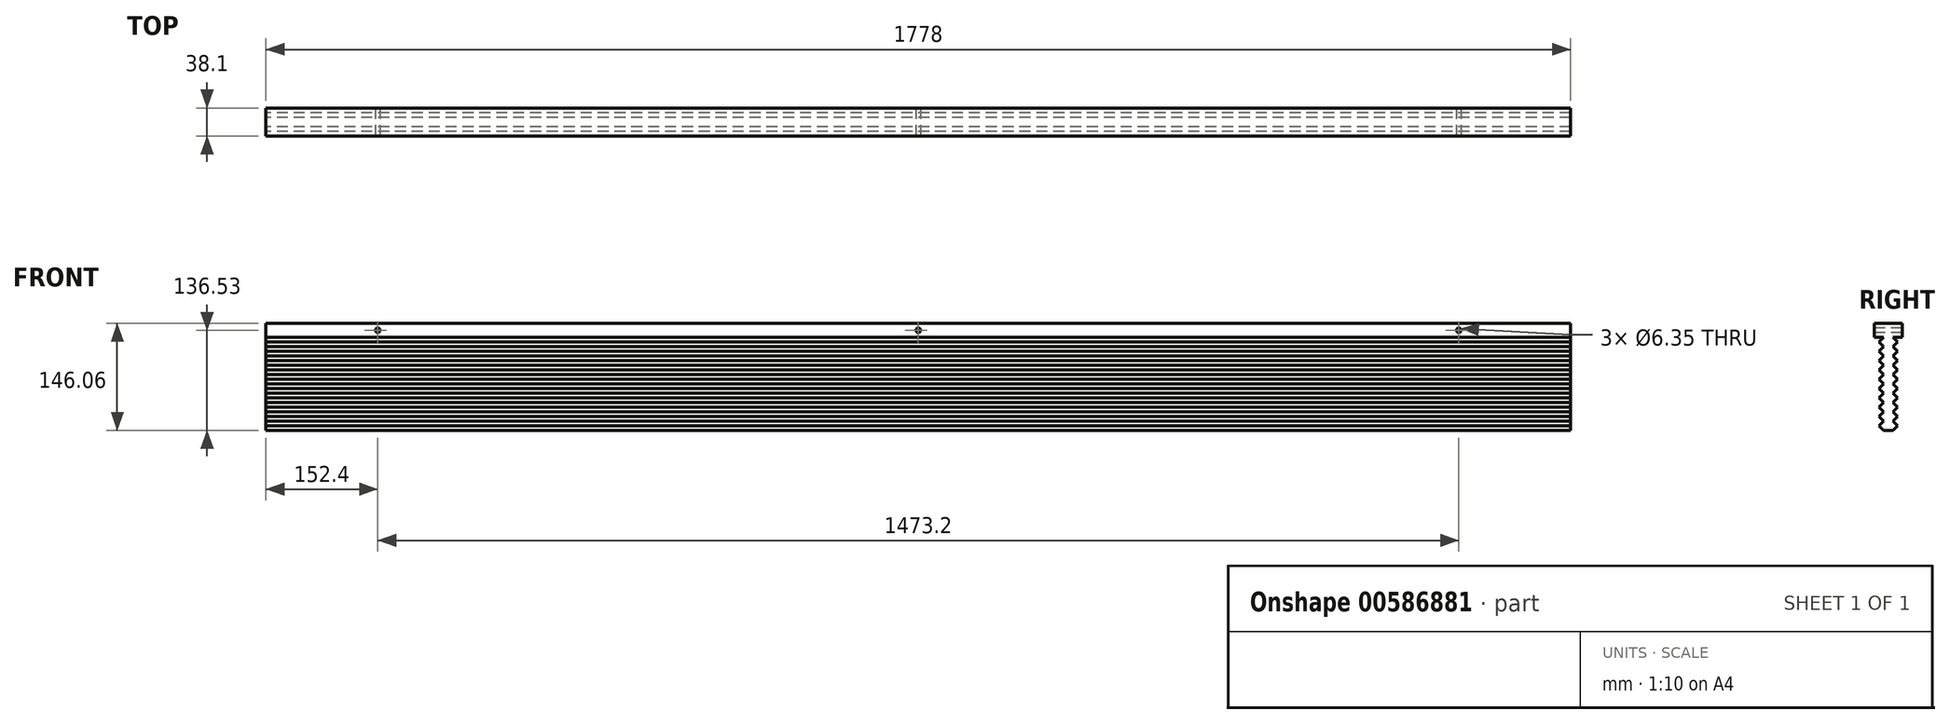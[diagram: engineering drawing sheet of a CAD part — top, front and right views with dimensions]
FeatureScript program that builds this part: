
annotation { "Feature Type Name" : "Feature", "Feature Type Description" : "" }
export const myFeature = defineFeature(function(context is Context, id is Id, definition is map)
    precondition{}
    {
        {
            var Q0;
            Q0=qCreatedBy(makeId("Right.planeOp"),FACE);
            var sketch = newSketch(context, id + "F0", { "sketchPlane" : qUnion([Q0])});
            skLineSegment(sketch, "E0.bottom", {"start": v(-19.05, 9.52) * mm, "end": v(19.05, 9.52) * mm});
            skLineSegment(sketch, "E0.top", {"start": v(-19.05, -9.52) * mm, "end": v(19.05, -9.52) * mm});
            skLineSegment(sketch, "E0.left", {"start": v(-19.05, 9.52) * mm, "end": v(-19.05, -9.52) * mm});
            skLineSegment(sketch, "E0.right", {"start": v(19.05, 9.52) * mm, "end": v(19.05, -9.52) * mm});
            skPoint(sketch, "E0.middle", {"position": v(0, 0) * mm});
            skSolve(sketch);
        }
        {
            var Q0;
            Q0 = qSketchRegion(id + "F0", true);
            extrude(context, id + "F1", {"entities" : qUnion([Q0]), "endBound" : BoundingType.SYMMETRIC, "depth" : 1778 * mm, "offsetDistance" : 25.4 * mm});
        }
        {
            var Q0;
            Q0=qCreatedBy(makeId("Right.planeOp"),FACE);
            var sketch = newSketch(context, id + "F2", { "sketchPlane" : qUnion([Q0])});
            skLineSegment(sketch, "E1", {"start": v(-6.35, -9.52) * mm, "end": v(-12.7, -15.88) * mm});
            skLineSegment(sketch, "E2", {"start": v(-12.7, -15.87) * mm, "end": v(-6.35, -22.22) * mm});
            skLineSegment(sketch, "E3", {"start": v(-6.35, -22.23) * mm, "end": v(0, -22.23) * mm});
            skLineSegment(sketch, "E4", {"start": v(-6.35, -9.52) * mm, "end": v(0, -9.52) * mm});
            skLineSegment(sketch, "E5.MirrorCS", {"start": v(6.35, -9.52) * mm, "end": v(0, -9.52) * mm});
            skLineSegment(sketch, "E6.MirrorCS", {"start": v(6.35, -9.52) * mm, "end": v(12.7, -15.88) * mm});
            skLineSegment(sketch, "E7.MirrorCS", {"start": v(12.7, -15.87) * mm, "end": v(6.35, -22.23) * mm});
            skLineSegment(sketch, "E8.MirrorCS", {"start": v(6.35, -22.23) * mm, "end": v(0, -22.23) * mm});
            skLineSegment(sketch, "E9.1.0.0", {"start": v(-6.35, -34.93) * mm, "end": v(0, -34.93) * mm});
            skLineSegment(sketch, "E9.1.0.1", {"start": v(-12.7, -28.57) * mm, "end": v(-6.35, -34.92) * mm});
            skLineSegment(sketch, "E9.1.0.2", {"start": v(-6.35, -22.22) * mm, "end": v(-12.7, -28.57) * mm});
            skLineSegment(sketch, "E9.1.0.5", {"start": v(6.35, -22.22) * mm, "end": v(12.7, -28.57) * mm});
            skLineSegment(sketch, "E9.1.0.6", {"start": v(12.7, -28.57) * mm, "end": v(6.35, -34.93) * mm});
            skLineSegment(sketch, "E9.1.0.7", {"start": v(6.35, -34.93) * mm, "end": v(0, -34.93) * mm});
            skLineSegment(sketch, "E9.2.0.0", {"start": v(-6.35, -47.63) * mm, "end": v(0, -47.63) * mm});
            skLineSegment(sketch, "E9.2.0.1", {"start": v(-12.7, -41.27) * mm, "end": v(-6.35, -47.62) * mm});
            skLineSegment(sketch, "E9.2.0.2", {"start": v(-6.35, -34.92) * mm, "end": v(-12.7, -41.28) * mm});
            skLineSegment(sketch, "E9.2.0.3", {"start": v(-6.35, -34.93) * mm, "end": v(0, -34.93) * mm});
            skLineSegment(sketch, "E9.2.0.4", {"start": v(6.35, -34.93) * mm, "end": v(0, -34.93) * mm});
            skLineSegment(sketch, "E9.2.0.5", {"start": v(6.35, -34.92) * mm, "end": v(12.7, -41.27) * mm});
            skLineSegment(sketch, "E9.2.0.6", {"start": v(12.7, -41.28) * mm, "end": v(6.35, -47.63) * mm});
            skLineSegment(sketch, "E9.2.0.7", {"start": v(6.35, -47.63) * mm, "end": v(0, -47.63) * mm});
            skLineSegment(sketch, "E9.direction1", {"start": v(-6.35, -22.23) * mm, "end": v(-6.35, -34.93) * mm, "construction": true});
            skLineSegment(sketch, "E10.0.3.0", {"start": v(-6.35, -60.33) * mm, "end": v(0, -60.33) * mm});
            skLineSegment(sketch, "E10.3.3.0", {"start": v(-12.7, -53.97) * mm, "end": v(-6.35, -60.32) * mm});
            skLineSegment(sketch, "E10.6.3.0", {"start": v(-6.35, -47.62) * mm, "end": v(-12.7, -53.97) * mm});
            skLineSegment(sketch, "E10.9.3.0", {"start": v(-6.35, -47.62) * mm, "end": v(0, -47.62) * mm});
            skLineSegment(sketch, "E10.12.3.0", {"start": v(6.35, -47.62) * mm, "end": v(0, -47.62) * mm});
            skLineSegment(sketch, "E10.15.3.0", {"start": v(6.35, -47.62) * mm, "end": v(12.7, -53.97) * mm});
            skLineSegment(sketch, "E10.18.3.0", {"start": v(12.7, -53.97) * mm, "end": v(6.35, -60.32) * mm});
            skLineSegment(sketch, "E10.21.3.0", {"start": v(6.35, -60.33) * mm, "end": v(0, -60.33) * mm});
            skLineSegment(sketch, "E10.0.4.0", {"start": v(-6.35, -73.03) * mm, "end": v(0, -73.03) * mm});
            skLineSegment(sketch, "E10.3.4.0", {"start": v(-12.7, -66.67) * mm, "end": v(-6.35, -73.02) * mm});
            skLineSegment(sketch, "E10.6.4.0", {"start": v(-6.35, -60.32) * mm, "end": v(-12.7, -66.67) * mm});
            skLineSegment(sketch, "E10.9.4.0", {"start": v(-6.35, -60.32) * mm, "end": v(0, -60.32) * mm});
            skLineSegment(sketch, "E10.12.4.0", {"start": v(6.35, -60.32) * mm, "end": v(0, -60.32) * mm});
            skLineSegment(sketch, "E10.15.4.0", {"start": v(6.35, -60.32) * mm, "end": v(12.7, -66.67) * mm});
            skLineSegment(sketch, "E10.18.4.0", {"start": v(12.7, -66.67) * mm, "end": v(6.35, -73.03) * mm});
            skLineSegment(sketch, "E10.21.4.0", {"start": v(6.35, -73.03) * mm, "end": v(0, -73.03) * mm});
            skLineSegment(sketch, "E10.0.5.0", {"start": v(-6.35, -85.73) * mm, "end": v(0, -85.73) * mm});
            skLineSegment(sketch, "E10.3.5.0", {"start": v(-12.7, -79.38) * mm, "end": v(-6.35, -85.72) * mm});
            skLineSegment(sketch, "E10.6.5.0", {"start": v(-6.35, -73.03) * mm, "end": v(-12.7, -79.38) * mm});
            skLineSegment(sketch, "E10.9.5.0", {"start": v(-6.35, -73.03) * mm, "end": v(0, -73.03) * mm});
            skLineSegment(sketch, "E10.12.5.0", {"start": v(6.35, -73.03) * mm, "end": v(0, -73.03) * mm});
            skLineSegment(sketch, "E10.15.5.0", {"start": v(6.35, -73.03) * mm, "end": v(12.7, -79.38) * mm});
            skLineSegment(sketch, "E10.18.5.0", {"start": v(12.7, -79.38) * mm, "end": v(6.35, -85.72) * mm});
            skLineSegment(sketch, "E10.21.5.0", {"start": v(6.35, -85.73) * mm, "end": v(0, -85.73) * mm});
            skLineSegment(sketch, "E10.0.6.0", {"start": v(-6.35, -98.42) * mm, "end": v(0, -98.42) * mm});
            skLineSegment(sketch, "E10.3.6.0", {"start": v(-12.7, -92.07) * mm, "end": v(-6.35, -98.42) * mm});
            skLineSegment(sketch, "E10.6.6.0", {"start": v(-6.35, -85.72) * mm, "end": v(-12.7, -92.07) * mm});
            skLineSegment(sketch, "E10.9.6.0", {"start": v(-6.35, -85.72) * mm, "end": v(0, -85.72) * mm});
            skLineSegment(sketch, "E10.12.6.0", {"start": v(6.35, -85.72) * mm, "end": v(0, -85.72) * mm});
            skLineSegment(sketch, "E10.15.6.0", {"start": v(6.35, -85.72) * mm, "end": v(12.7, -92.07) * mm});
            skLineSegment(sketch, "E10.18.6.0", {"start": v(12.7, -92.07) * mm, "end": v(6.35, -98.42) * mm});
            skLineSegment(sketch, "E10.21.6.0", {"start": v(6.35, -98.42) * mm, "end": v(0, -98.42) * mm});
            skLineSegment(sketch, "E10.0.7.0", {"start": v(-6.35, -111.12) * mm, "end": v(0, -111.12) * mm});
            skLineSegment(sketch, "E10.3.7.0", {"start": v(-12.7, -104.77) * mm, "end": v(-6.35, -111.12) * mm});
            skLineSegment(sketch, "E10.6.7.0", {"start": v(-6.35, -98.42) * mm, "end": v(-12.7, -104.77) * mm});
            skLineSegment(sketch, "E10.9.7.0", {"start": v(-6.35, -98.42) * mm, "end": v(0, -98.42) * mm});
            skLineSegment(sketch, "E10.12.7.0", {"start": v(6.35, -98.42) * mm, "end": v(0, -98.42) * mm});
            skLineSegment(sketch, "E10.15.7.0", {"start": v(6.35, -98.42) * mm, "end": v(12.7, -104.77) * mm});
            skLineSegment(sketch, "E10.18.7.0", {"start": v(12.7, -104.77) * mm, "end": v(6.35, -111.12) * mm});
            skLineSegment(sketch, "E10.21.7.0", {"start": v(6.35, -111.12) * mm, "end": v(0, -111.12) * mm});
            skLineSegment(sketch, "E10.0.8.0", {"start": v(-6.35, -123.83) * mm, "end": v(0, -123.83) * mm});
            skLineSegment(sketch, "E10.3.8.0", {"start": v(-12.7, -117.47) * mm, "end": v(-6.35, -123.82) * mm});
            skLineSegment(sketch, "E10.6.8.0", {"start": v(-6.35, -111.12) * mm, "end": v(-12.7, -117.47) * mm});
            skLineSegment(sketch, "E10.9.8.0", {"start": v(-6.35, -111.12) * mm, "end": v(0, -111.12) * mm});
            skLineSegment(sketch, "E10.12.8.0", {"start": v(6.35, -111.12) * mm, "end": v(0, -111.12) * mm});
            skLineSegment(sketch, "E10.15.8.0", {"start": v(6.35, -111.12) * mm, "end": v(12.7, -117.47) * mm});
            skLineSegment(sketch, "E10.18.8.0", {"start": v(12.7, -117.47) * mm, "end": v(6.35, -123.82) * mm});
            skLineSegment(sketch, "E10.21.8.0", {"start": v(6.35, -123.83) * mm, "end": v(0, -123.83) * mm});
            skLineSegment(sketch, "E10.0.9.0", {"start": v(-6.35, -136.53) * mm, "end": v(0, -136.53) * mm});
            skLineSegment(sketch, "E10.3.9.0", {"start": v(-12.7, -130.17) * mm, "end": v(-6.35, -136.53) * mm});
            skLineSegment(sketch, "E10.6.9.0", {"start": v(-6.35, -123.82) * mm, "end": v(-12.7, -130.18) * mm});
            skLineSegment(sketch, "E10.9.9.0", {"start": v(-6.35, -123.82) * mm, "end": v(0, -123.82) * mm});
            skLineSegment(sketch, "E10.12.9.0", {"start": v(6.35, -123.82) * mm, "end": v(0, -123.82) * mm});
            skLineSegment(sketch, "E10.15.9.0", {"start": v(6.35, -123.82) * mm, "end": v(12.7, -130.18) * mm});
            skLineSegment(sketch, "E10.18.9.0", {"start": v(12.7, -130.17) * mm, "end": v(6.35, -136.53) * mm});
            skLineSegment(sketch, "E10.21.9.0", {"start": v(6.35, -136.53) * mm, "end": v(0, -136.53) * mm});
            skSolve(sketch);
        }
        {
            var Q0;
            Q0 = qSketchRegion(id + "F2", true);
            extrude(context, id + "F3", {"entities" : qUnion([Q0]), "operationType" : NewBodyOperationType.ADD, "endBound" : BoundingType.SYMMETRIC, "depth" : 1778 * mm, "offsetDistance" : 25.4 * mm});
        }
        {
            var Q0;
            Q0=makeQuery(id+"F1.opExtrude","SWEPT_FACE",FACE,{"disambiguationData":[OSD([sQuery(id+"F0.wireOp",EDGE,"E0.left")])]});
            var sketch = newSketch(context, id + "F4", { "sketchPlane" : qUnion([Q0])});
            skPoint(sketch, "E11", {"position": v(0, 0) * mm});
            skPoint(sketch, "E12", {"position": v(-736.6, 0) * mm});
            skPoint(sketch, "E13", {"position": v(736.6, 0) * mm});
            skSolve(sketch);
        }
        {
            var Q0;
            Q0=sQuery(id+"F4.wireOp",VERTEX,"E11");
            var Q1;
            Q1=sQuery(id+"F4.wireOp",VERTEX,"E13");
            var Q2;
            Q2=sQuery(id+"F4.wireOp",VERTEX,"E12");
            var Q3;
            Q3=makeQuery(id+"F1.opExtrude","SWEPT_BODY",BODY,{"disambiguationData":[OSD([sQuery(id+"F0.wireOp",EDGE,"E0.bottom"),sQuery(id+"F0.wireOp",EDGE,"E0.top"),sQuery(id+"F0.wireOp",EDGE,"E0.left"),sQuery(id+"F0.wireOp",EDGE,"E0.right")])]});
            hole(context, id + "F5", {"style" : HoleStyle.SIMPLE, "endStyle" : HoleEndStyle.THROUGH, "holeDiameter" : 6.35 * mm, "majorDiameter" : 6.35 * mm, "isTappedThrough" : true, "tappedDepth" : 12.7 * mm, "tapClearance" : 3, "locations" : qUnion([Q0, Q1, Q2]), "scope" : qUnion([Q3])});
        }
    });
